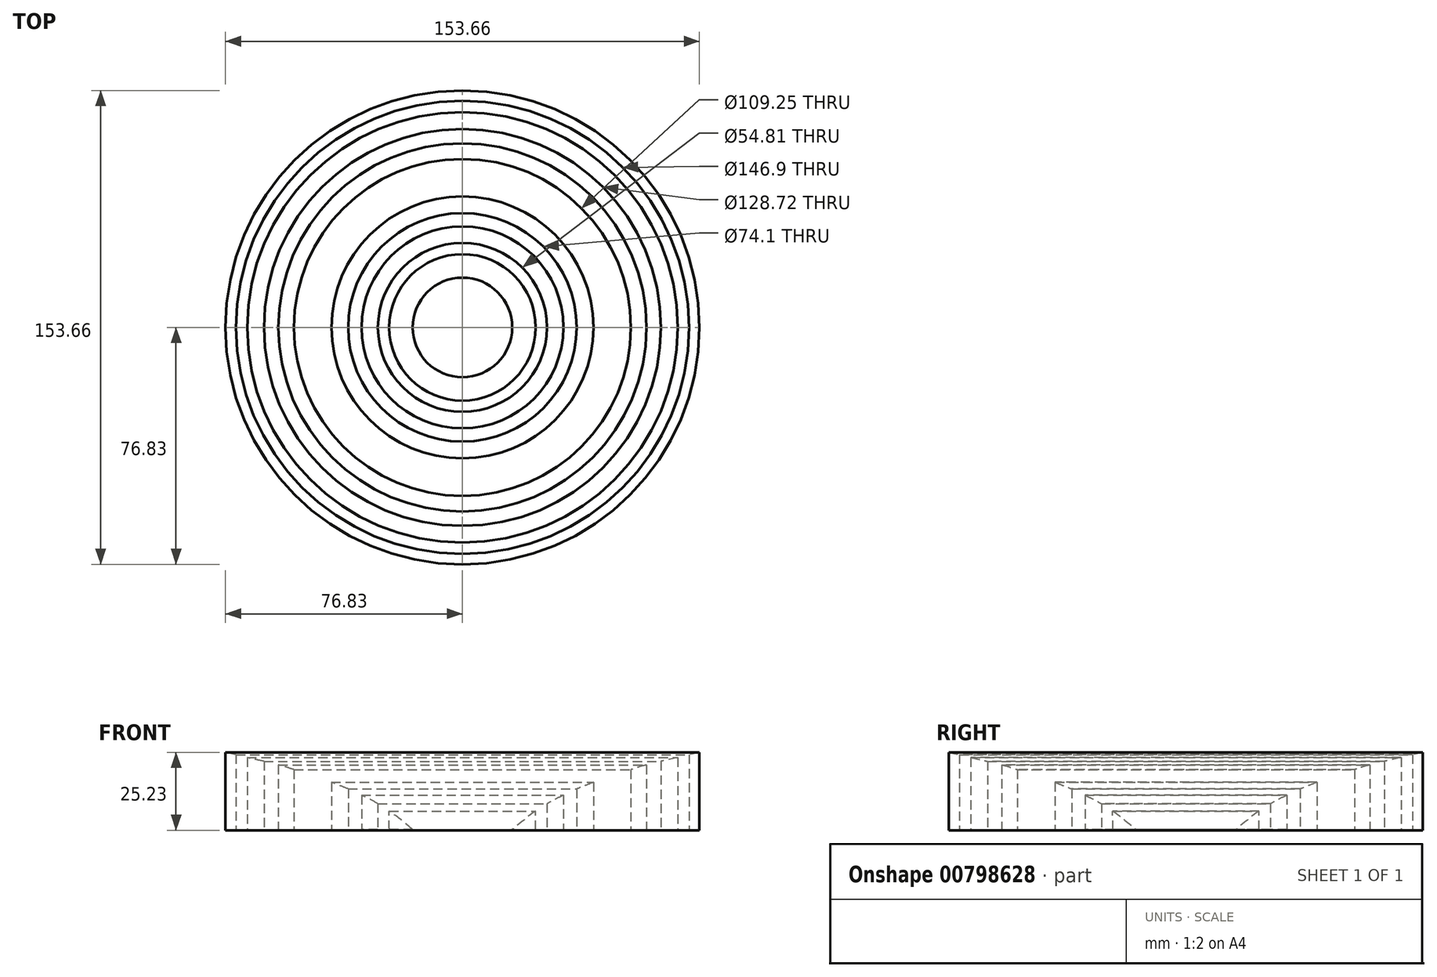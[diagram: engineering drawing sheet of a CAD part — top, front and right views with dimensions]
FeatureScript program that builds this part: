
annotation { "Feature Type Name" : "Feature", "Feature Type Description" : "" }
export const myFeature = defineFeature(function(context is Context, id is Id, definition is map)
    precondition{}
    {
        {
            var Q0;
            Q0=qCreatedBy(makeId("Front.planeOp"),FACE);
            var sketch = newSketch(context, id + "F0", { "sketchPlane" : qUnion([Q0])});
            skPoint(sketch, "E0", {"position": v(16.14, 1.56) * mm});
            skPoint(sketch, "E1", {"position": v(17.72, 2.9) * mm});
            skPoint(sketch, "E2", {"position": v(19.43, 4.3) * mm});
            skPoint(sketch, "E3", {"position": v(21.24, 5.78) * mm});
            skPoint(sketch, "E4", {"position": v(22.54, 6.75) * mm});
            skPoint(sketch, "E5", {"position": v(23.74, 7.59) * mm});
            skPoint(sketch, "E6", {"position": v(25.37, 8.65) * mm});
            skPoint(sketch, "E7", {"position": v(26.43, 9.4) * mm});
            skPoint(sketch, "E8", {"position": v(27.4, 10) * mm});
            skPoint(sketch, "E9", {"position": v(28.38, 10.55) * mm});
            skPoint(sketch, "E10", {"position": v(29.77, 11.25) * mm});
            skPoint(sketch, "E11", {"position": v(30.6, 11.76) * mm});
            skPoint(sketch, "E12", {"position": v(31.49, 12.08) * mm});
            skPoint(sketch, "E13", {"position": v(32.74, 12.73) * mm});
            skPoint(sketch, "E14", {"position": v(34.6, 13.61) * mm});
            skPoint(sketch, "E15", {"position": v(35.52, 14.12) * mm});
            skPoint(sketch, "E16", {"position": v(37.05, 14.82) * mm});
            skPoint(sketch, "E17", {"position": v(38.95, 15.51) * mm});
            skPoint(sketch, "E18", {"position": v(41, 16.35) * mm});
            skPoint(sketch, "E19", {"position": v(42.48, 16.9) * mm});
            skPoint(sketch, "E20", {"position": v(43.91, 17.42) * mm});
            skPoint(sketch, "E21", {"position": v(45.44, 18.07) * mm});
            skPoint(sketch, "E22", {"position": v(46.6, 18.48) * mm});
            skPoint(sketch, "E23", {"position": v(47.44, 18.71) * mm});
            skPoint(sketch, "E24", {"position": v(48.74, 19.36) * mm});
            skPoint(sketch, "E25", {"position": v(49.38, 19.46) * mm});
            skPoint(sketch, "E26", {"position": v(50.27, 19.78) * mm});
            skPoint(sketch, "E27", {"position": v(50.91, 19.83) * mm});
            skPoint(sketch, "E28", {"position": v(53.05, 20.66) * mm});
            skPoint(sketch, "E29", {"position": v(54.62, 20.99) * mm});
            skPoint(sketch, "E30", {"position": v(56.76, 21.36) * mm});
            skPoint(sketch, "E31", {"position": v(58.1, 22.15) * mm});
            skPoint(sketch, "E32", {"position": v(59.68, 22.42) * mm});
            skPoint(sketch, "E33", {"position": v(61.72, 22.98) * mm});
            skPoint(sketch, "E34", {"position": v(62.88, 23.17) * mm});
            skPoint(sketch, "E35", {"position": v(64.36, 23.72) * mm});
            skPoint(sketch, "E36", {"position": v(65.7, 24.1) * mm});
            skPoint(sketch, "E37", {"position": v(67.98, 24.46) * mm});
            skPoint(sketch, "E38", {"position": v(69.79, 24.83) * mm});
            skPoint(sketch, "E39", {"position": v(71.87, 25.44) * mm});
            skPoint(sketch, "E40", {"position": v(73.45, 25.72) * mm});
            skPoint(sketch, "E41", {"position": v(75.35, 26.32) * mm});
            skPoint(sketch, "E42", {"position": v(76.83, 26.6) * mm});
            skPoint(sketch, "E43", {"position": v(78.78, 26.83) * mm});
            skPoint(sketch, "E44", {"position": v(80.5, 27.38) * mm});
            skFitSpline(sketch, "E45", {"points": [v(16.14, 1.56) * mm, v(17.72, 2.9) * mm, v(19.43, 4.3) * mm, v(21.24, 5.78) * mm, v(22.54, 6.75) * mm, v(23.74, 7.59) * mm, v(25.37, 8.65) * mm, v(26.43, 9.4) * mm, v(29.77, 11.25) * mm, v(32.74, 12.73) * mm, v(35.52, 14.12) * mm, v(38.95, 15.51) * mm, v(42.48, 16.9) * mm, v(46.6, 18.48) * mm, v(50.91, 19.83) * mm, v(54.62, 20.99) * mm, v(58.1, 22.15) * mm, v(61.72, 22.98) * mm, v(64.36, 23.72) * mm, v(67.98, 24.46) * mm, v(71.87, 25.44) * mm, v(75.35, 26.32) * mm, v(78.78, 26.83) * mm, v(80.5, 26.83) * mm], "startDerivative": vector(42.75, 37.28) * mm, "endDerivative": vector(47.04, -2) * mm});
            skLineSegment(sketch, "E46", {"start": v(80.5, 26.83) * mm, "end": v(80.5, 1.35) * mm});
            skLineSegment(sketch, "E47", {"start": v(80.5, 1.35) * mm, "end": v(16.14, 1.56) * mm});
            skLineSegment(sketch, "E48", {"start": v(0, 1.54) * mm, "end": v(0, 32.24) * mm});
            skLineSegment(sketch, "E49", {"start": v(0, 1.54) * mm, "end": v(0.07, 1.54) * mm});
            skLineSegment(sketch, "E50", {"start": v(0.07, 1.54) * mm, "end": v(0, 32.24) * mm});
            skLineSegment(sketch, "E51", {"start": v(32.74, 12.73) * mm, "end": v(32.74, 1.56) * mm});
            skLineSegment(sketch, "E52", {"start": v(49.38, 19.46) * mm, "end": v(49.38, 1.45) * mm});
            skLineSegment(sketch, "E53", {"start": v(64.36, 23.72) * mm, "end": v(64.36, 1.4) * mm});
            skLineSegment(sketch, "E54", {"start": v(23.74, 7.59) * mm, "end": v(23.72, 0) * mm});
            skLineSegment(sketch, "E55", {"start": v(37.05, 14.82) * mm, "end": v(37.05, 1.49) * mm});
            skLineSegment(sketch, "E56", {"start": v(42.48, 16.9) * mm, "end": v(42.48, 1.47) * mm});
            skLineSegment(sketch, "E57", {"start": v(54.62, 20.99) * mm, "end": v(54.62, 1.43) * mm});
            skLineSegment(sketch, "E58", {"start": v(59.68, 22.42) * mm, "end": v(59.68, 1.42) * mm});
            skLineSegment(sketch, "E59", {"start": v(45.44, 18.07) * mm, "end": v(45.44, 1.46) * mm});
            skLineSegment(sketch, "E60", {"start": v(69.79, 24.83) * mm, "end": v(69.79, 1.39) * mm});
            skLineSegment(sketch, "E61", {"start": v(73.45, 25.72) * mm, "end": v(73.45, 1.37) * mm});
            skLineSegment(sketch, "E62", {"start": v(76.83, 26.6) * mm, "end": v(76.83, 1.36) * mm});
            skLineSegment(sketch, "E63", {"start": v(27.4, 10) * mm, "end": v(27.4, 1.52) * mm});
            skLineSegment(sketch, "E64", {"start": v(32.74, 12.73) * mm, "end": v(32.74, -1.63) * mm});
            skLineSegment(sketch, "E65", {"start": v(54.62, 20.99) * mm, "end": v(54.62, -5.2) * mm});
            skLineSegment(sketch, "E66", {"start": v(59.68, 22.42) * mm, "end": v(59.68, -0.92) * mm});
            skLineSegment(sketch, "E67", {"start": v(59.68, 20.72) * mm, "end": v(59.68, 23.49) * mm});
            skLineSegment(sketch, "E68", {"start": v(69.79, 22.68) * mm, "end": v(69.79, 27.13) * mm});
            skLineSegment(sketch, "E69", {"start": v(69.79, 27.13) * mm, "end": v(69.79, 0.64) * mm});
            skLineSegment(sketch, "E70", {"start": v(76.83, 20.52) * mm, "end": v(76.83, 30.9) * mm});
            skLineSegment(sketch, "E71", {"start": v(73.45, 21.35) * mm, "end": v(73.45, 28.52) * mm});
            skSolve(sketch);
        }
        {
            var Q0;
            Q0=qCreatedBy(makeId("Top.planeOp"),FACE);
            var sketch = newSketch(context, id + "F1", { "sketchPlane" : qUnion([Q0])});
            skCircle(sketch, "E72", {"center": v(0, 0) * mm, "radius": 82.55 * mm});
            skCircle(sketch, "E73", {"center": v(0, 0) * mm, "radius": 12.7 * mm});
            skSolve(sketch);
        }
        {
            var Q0;
            {var subQ0=sQuery(id+"F0.wireOp",EDGE,"E47");var subQ1=sQuery(id+"F0.wireOp",EDGE,"E45");var subQ2=makeQuery(id+"F0.imprint","INTERSECT",VERTEX,{"derivedFrom":[subQ1,subQ0]});Q0=makeQuery(id+"F0.imprint","IMPRINT",FACE,{"disambiguationData":[TD([[makeQuery(id+"F0.imprint","IMPRINT",EDGE,{"disambiguationData":[TD([[subQ2,-1.0]])],"derivedFrom":subQ1}),-1.0]])]});}
            var Q1;
            {var subQ5=sQuery(id+"F0.wireOp",EDGE,"E64");var subQ7=makeQuery(id+"F0.imprint","IMPRINT",VERTEX,{"derivedFrom":subQ5});Q1=makeQuery(id+"F0.imprint","IMPRINT",FACE,{"disambiguationData":[TD([[makeQuery(id+"F0.imprint","IMPRINT",EDGE,{"disambiguationData":[TD([[subQ7,1.0]])],"derivedFrom":subQ5}),-1.0]])]});}
            var Q2;
            {var subQ0=sQuery(id+"F0.wireOp",EDGE,"E56");Q2=makeQuery(id+"F0.imprint","IMPRINT",FACE,{"disambiguationData":[TD([[makeQuery(id+"F0.imprint","IMPRINT",EDGE,{"derivedFrom":subQ0}),-1.0]])]});}
            var Q3;
            {var subQ0=sQuery(id+"F0.wireOp",EDGE,"E59");Q3=makeQuery(id+"F0.imprint","IMPRINT",FACE,{"disambiguationData":[TD([[makeQuery(id+"F0.imprint","IMPRINT",EDGE,{"derivedFrom":subQ0}),1.0]])]});}
            var Q4;
            {var subQ0=sQuery(id+"F0.wireOp",EDGE,"E67");var subQ10=makeQuery(id+"F0.imprint","IMPRINT",VERTEX,{"derivedFrom":subQ0});Q4=makeQuery(id+"F0.imprint","IMPRINT",FACE,{"disambiguationData":[TD([[makeQuery(id+"F0.imprint","IMPRINT",EDGE,{"disambiguationData":[TD([[subQ10,1.0]])],"derivedFrom":subQ0}),1.0]])]});}
            var Q5;
            {var subQ4=sQuery(id+"F0.wireOp",EDGE,"E53");Q5=makeQuery(id+"F0.imprint","IMPRINT",FACE,{"disambiguationData":[TD([[makeQuery(id+"F0.imprint","IMPRINT",EDGE,{"derivedFrom":subQ4}),1.0]])]});}
            var Q6;
            {var subQ4=sQuery(id+"F0.wireOp",EDGE,"E61");Q6=makeQuery(id+"F0.imprint","IMPRINT",FACE,{"disambiguationData":[TD([[makeQuery(id+"F0.imprint","IMPRINT",EDGE,{"derivedFrom":subQ4}),1.0]])]});}
            var Q7;
            Q7=sQuery(id+"F0.wireOp",EDGE,"E48");
            revolve(context, id + "F2", {"surfaceOperationType" : NewSurfaceOperationType.NEW, "entities" : qUnion([Q0, Q1, Q2, Q3, Q4, Q5, Q6]), "axis" : qUnion([Q7]), "revolveType" : RevolveType.FULL});
        }
    });
